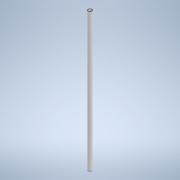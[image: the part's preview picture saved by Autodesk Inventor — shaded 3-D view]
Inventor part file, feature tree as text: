
AUTODESK INVENTOR PART (.ipt)
format: ipt  version: 2022 (Build 260153000, 153)  size: 93,184 bytes
history: native  units: mm
features: extrude x1, sketch x1
ambient origin geometry x8: Origin, YZ Plane, XZ Plane, XY Plane, X Axis, Y Axis, Z Axis, Center Point
bodies: Body1 (feature_tree)
feature tree (2):
  extrude  "Extrusion2"  Depth=500.0mm TaperAngle=0.0deg
  sketch  "Sketch2"  dims[d4=14.0mm d5=500.0mm d6=0.0mm d7=12.0mm]
